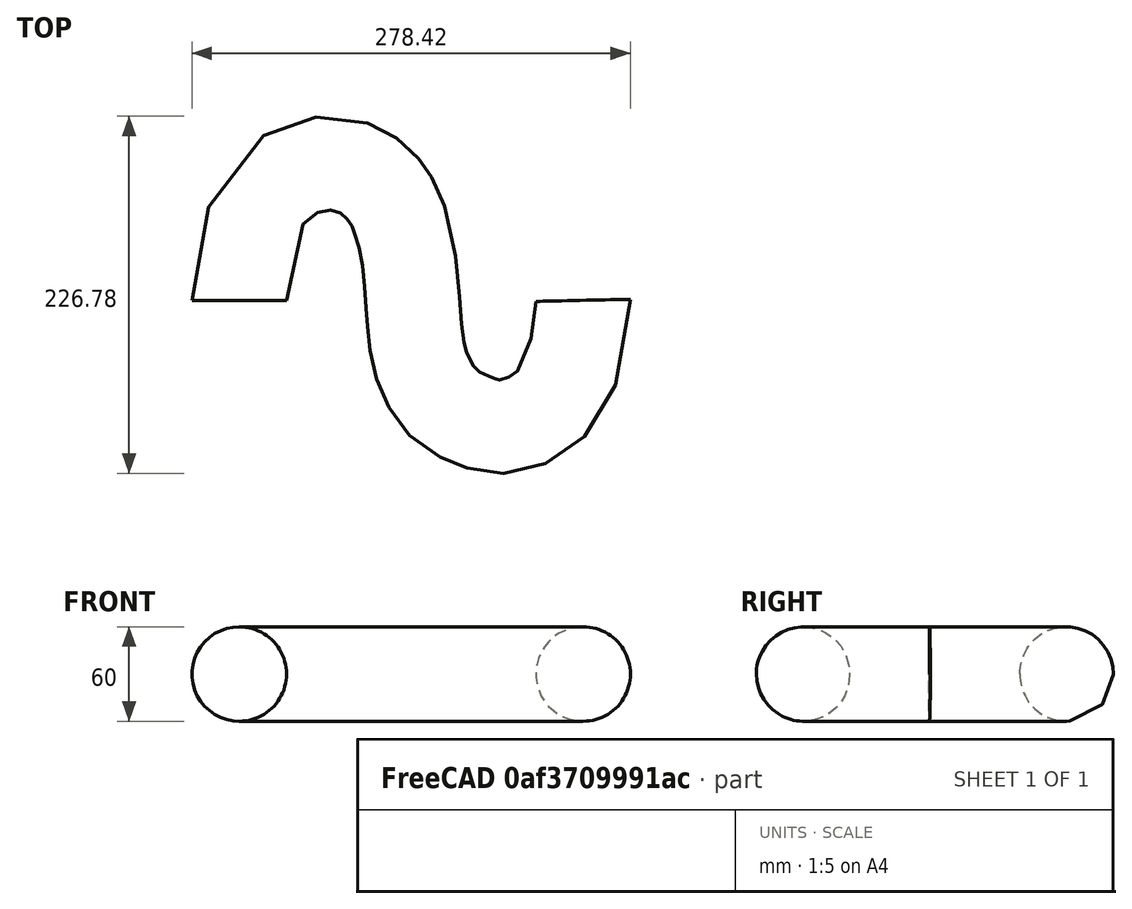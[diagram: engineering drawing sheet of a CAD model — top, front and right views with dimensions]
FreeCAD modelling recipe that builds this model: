
FCSTD DOCUMENT  (FreeCAD 0.19R24291 (Git))
Label: sBendPipe
License: All rights reserved
LicenseURL: http://en.wikipedia.org/wiki/All_rights_reserved
objects: Part::Feature×3, Sketcher::SketchObject×2, PartDesign::AdditivePipe×1, PartDesign::Body×1, Part::Cut×1
note: 9 computed .brp shape members not serialized (recipe doc carries the construction recipe); baked Part::Feature solids carry a one-line shape summary decoded from their .brp

FEATURE [Sketcher::SketchObject] Sketch  label="Circular Patch"
  FullyConstrained = true
  MapMode = 5
  Placement = pos=(0,0,0) rot=(1,0,0;1.5708rad)
  Support = -> [XZ_Plane]
  sketch-geometry (1):
    g0: Circle CenterX=0 CenterY=0 CenterZ=0 NormalX=0 NormalY=0 NormalZ=1 AngleXU=0 Radius=30
  constraints (2):
    c: Coincident(g0,g-1)
    c: Radius(g0) = 30
FEATURE [Sketcher::SketchObject] Sketch001  label="Pipe Wall Sweep"
  FullyConstrained = false
  MapMode = 5
  Support = -> [XY_Plane]
  sketch-geometry (39):
    g0-g19: Circle x20 (B-spline internal-alignment scaffolding for g20; pole/knot coordinates omitted)
    g20: BSplineCurve PolesCount=20 KnotsCount=18 Degree=3 IsPeriodic=0
    g21-g38: GeomPoint x18 (B-spline internal-alignment scaffolding for g20; pole/knot coordinates omitted)
  constraints (6):
    c: Coincident(g20,g-1)
    c: Weight(g0) = 1
    c: Equal(g0, g1-g19) x19
    c: PointOnObject(g20,g-1)
    c: InternalAlignment(g0-g19 -> g20) x20
    c: InternalAlignment(g21-g38 -> g20) x18
FEATURE [PartDesign::AdditivePipe] AdditivePipe
  AuxilleryCurvelinear = true
  AuxillerySpineTangent = false
  Binormal = (0,0,0)
  Mode = 0
  Placement = pos=(0,0,0) rot=(1,0,0;1.5708rad)
  Profile = -> Sketch
  Spine = -> Sketch001
  SpineTangent = false
  Transformation = 0
  Transition = 0
FEATURE [PartDesign::Body] Body
  Group = -> [Sketch,Sketch001,AdditivePipe]
  Origin = -> Origin
  Tip = -> AdditivePipe
FEATURE [Part::Feature] Face  label="inlet"
  shape: bbox 84.41 x 2.006e-07 x 65.04 mm, 1 faces, 0 solids (baked)
FEATURE [Part::Feature] Face001  label="outlet"
  shape: bbox 84.39 x 1.854 x 65.04 mm, 1 faces, 0 solids (baked)
FEATURE [Part::Feature] Shell
  shape: bbox 330.9 x 279.7 x 114 mm, 2 faces, 0 solids (baked)
FEATURE [Part::Cut] Cut
  Base = -> Shell
  Tool = -> Face001
